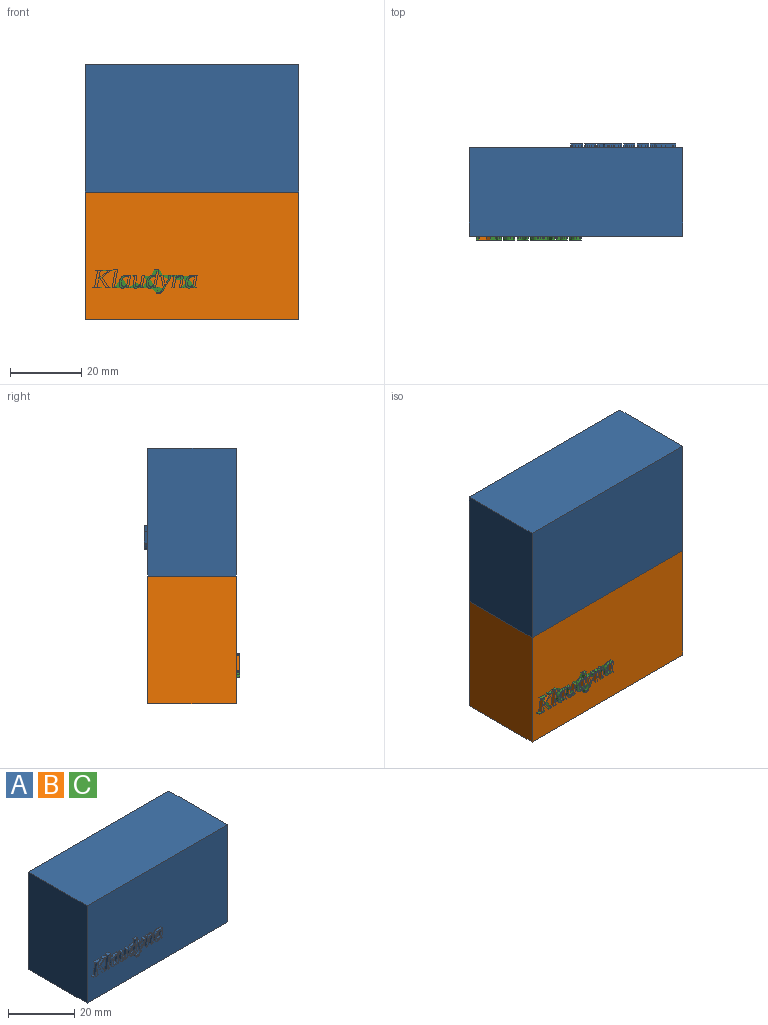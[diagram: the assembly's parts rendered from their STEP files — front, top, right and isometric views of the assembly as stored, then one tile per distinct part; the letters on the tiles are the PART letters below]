
ASSEMBLY  parts=3 mates=1
PART A: 191 faces, bbox 60x26x36 mm
  f0: plane 60x36mm, normal (0,-1,0), area 2104mm2, adj f1,f2,f3,f4,f6,f7,f8,f9
  f1: plane 60x25mm, normal (0,0,1), area 1500mm2, adj f0,f2,f4,f5
  f2: plane 36x25mm, normal (-1,0,0), area 900mm2, adj f0,f1,f3,f5
  f3: plane 60x25mm, normal (0,0,-1), area 1500mm2, adj f0,f2,f4,f5
  f4: plane 36x25mm, normal (1,0,0), area 900mm2, adj f0,f1,f3,f5
  f5: plane 60x36mm, normal (0,1,0), area 2160mm2, adj f1,f2,f3,f4
  f6: plane 1.57x1mm, normal (0,0,1), area 1.6mm2, adj f0,f7,f31,f32
  f7: plane 1x0.2mm, normal (-0.98,0,0.18), area 0.2mm2, adj f0,f6,f8,f32
  f8: plane 1x0.44mm, normal (-0.21,0,-0.98), area 0.5mm2, adj f0,f7,f9,f32
  f9: plane 2.53x2.08mm, normal (-0.64,0,0.77), area 3.3mm2, adj f0,f8,f10,f32
  f10: plane 2.08x1mm, normal (0.98,0,-0.17), area 2.1mm2, adj f0,f9,f11,f32
  f11: plane 1x0.66mm, normal (0.15,0,-0.99), area 0.7mm2, adj f0,f10,f12,f32
  f12: plane 1x0.2mm, normal (0.98,0,-0.19), area 0.2mm2, adj f0,f11,f13,f32
  f13: plane 2x1mm, normal (0,0,1), area 2mm2, adj f0,f12,f14,f32
  f14: plane 1x0.2mm, normal (-0.98,0,0.19), area 0.2mm2, adj f0,f13,f15,f32
  f15: plane 1x0.63mm, normal (-0.15,0,-0.99), area 0.6mm2, adj f0,f14,f16,f32
  f16: plane 4.41x1mm, normal (-0.98,0,0.17), area 4.5mm2, adj f0,f15,f17,f32
  f17: plane 1x0.65mm, normal (-0.15,0,0.99), area 0.7mm2, adj f0,f16,f18,f32
  f18: plane 1x0.2mm, normal (-0.98,0,0.18), area 0.2mm2, adj f0,f17,f19,f32
  f19: plane 2.08x1mm, normal (0,0,-1), area 2.1mm2, adj f0,f18,f20,f32
  f20: plane 1x0.2mm, normal (0.98,0,-0.18), area 0.2mm2, adj f0,f19,f21,f32
  f21: plane 1x0.7mm, normal (0.14,0,0.99), area 0.7mm2, adj f0,f20,f22,f32
  f22: plane 1.82x1mm, normal (0.98,0,-0.18), area 1.9mm2, adj f0,f21,f23,f32
  f23: plane 1x0.53mm, normal (0.63,0,-0.77), area 0.7mm2, adj f0,f22,f24,f32
  f24: plane 2.56x1.53mm, normal (-0.86,0,-0.51), area 3mm2, adj f0,f23,f25,f32
  f25: plane 1.15x1mm, normal (0,0,-1), area 1.1mm2, adj f0,f24,f26,f32
  f26: plane 1x0.2mm, normal (0.98,0,-0.18), area 0.2mm2, adj f0,f25,f27,f32
  f27: plane 1x0.5mm, normal (0.2,0,0.98), area 0.5mm2, adj f0,f26,f28,f32
  f28: plane 2.71x1.67mm, normal (0.85,0,0.52), area 3.2mm2, adj f0,f27,f29,f32
  f29: plane 2.07x1.7mm, normal (0.63,0,-0.77), area 2.7mm2, adj f0,f28,f30,f32
  f30: plane 1x0.58mm, normal (0.16,0,-0.99), area 0.6mm2, adj f0,f29,f31,f32
  f31: plane 1x0.2mm, normal (0.98,0,-0.18), area 0.2mm2, adj f0,f6,f30,f32
  f32: plane 5.52x5mm, normal (0,-1,0), area 8.4mm2, adj f6,f7,f8,f9,f10,f11,f12,f13
  f33: plane 5.04x1mm, normal (0.98,0,-0.17), area 5.1mm2, adj f0,f34,f40,f41
  f34: plane 1.12x1mm, normal (0,0,1), area 1.1mm2, adj f0,f33,f35,f41
  f35: plane 1x0.17mm, normal (-0.98,0,0.17), area 0.2mm2, adj f0,f34,f36,f41
  f36: plane 1x0.48mm, normal (-0.18,0,-0.98), area 0.5mm2, adj f0,f35,f37,f41
  f37: plane 5.05x1mm, normal (-0.99,0,0.17), area 5.1mm2, adj f0,f36,f38,f41
  f38: plane 1.22x1mm, normal (0,0,-1), area 1.2mm2, adj f0,f37,f39,f41
  f39: plane 1x0.17mm, normal (0.98,0,-0.17), area 0.2mm2, adj f0,f38,f40,f41
  f40: plane 1x0.59mm, normal (0.16,0,0.99), area 0.6mm2, adj f0,f33,f39,f41
  f41: plane 5.3x1.55mm, normal (0,-1,0), area 3.5mm2, adj f33,f34,f35,f36,f37,f38,f39,f40
  f42: plane 3.31x1mm, normal (0.98,0,-0.18), area 3.4mm2, adj f0,f43,f64,f65
  f43: plane 1x0.2mm, normal (0,0,1), area 0.2mm2, adj f0,f42,f44,f65
  f44: plane 1x0.17mm, normal (-0.6,0,0.8), area 0.2mm2, adj f0,f43,f45,f65
  f45: extruded ~1x0.85mm, area 0.9mm2, adj f0,f44,f46,f65
  f46: extruded ~1.04x1mm, area 1.1mm2, adj f0,f45,f47,f65
  f47: extruded ~1x0.89mm, area 1.2mm2, adj f0,f46,f48,f65
  f48: extruded ~1.22x1mm, area 1.3mm2, adj f0,f47,f49,f65
  f49: extruded ~1x0.91mm, area 1mm2, adj f0,f48,f50,f65
  f50: extruded ~1x0.73mm, area 0.8mm2, adj f0,f49,f51,f65
  f51: extruded ~1.15x1mm, area 1.4mm2, adj f0,f50,f52,f65
  f52: plane 1x0.58mm, normal (-0.98,0,0.18), area 0.6mm2, adj f0,f51,f53,f65
  f53: plane 1.06x1mm, normal (0,0,-1), area 1.1mm2, adj f0,f52,f54,f65
  f54: plane 1x0.17mm, normal (0.98,0,-0.17), area 0.2mm2, adj f0,f53,f64,f65
  f55: plane 2.22x1mm, normal (-0.98,0,0.18), area 2.3mm2, adj f56,f63,f65,f66
  f56: extruded ~1x0.92mm, area 1.1mm2, adj f55,f57,f65,f66
  f57: extruded ~1x0.45mm, area 0.5mm2, adj f56,f58,f65,f66
  f58: extruded ~1x0.64mm, area 0.7mm2, adj f57,f59,f65,f66
  f59: extruded ~1x1mm, area 1mm2, adj f58,f60,f65,f66
  f60: extruded ~1x0.76mm, area 0.9mm2, adj f59,f61,f65,f66
  f61: extruded ~1x0.68mm, area 0.8mm2, adj f60,f62,f65,f66
  f62: extruded ~1x0.31mm, area 0.3mm2, adj f61,f63,f65,f66
  f63: extruded ~1x0.27mm, area 0.3mm2, adj f55,f62,f65,f66
  f64: plane 1x0.42mm, normal (0.22,0,0.98), area 0.4mm2, adj f0,f42,f54,f65
  f65: plane 3.68x3.31mm, normal (0,-1,0), area 5.3mm2, adj f42,f43,f44,f45,f46,f47,f48,f49
  f66: plane 2.92x1.94mm, normal (0,-1,0), area 4.1mm2, adj f55,f56,f57,f58,f59,f60,f61,f62
  f67: extruded ~1x0.62mm, area 0.6mm2, adj f0,f68,f88,f89
  f68: plane 2.17x1mm, normal (0.98,0,-0.17), area 2.2mm2, adj f0,f67,f69,f89
  f69: plane 1.05x1mm, normal (0,0,1), area 1mm2, adj f0,f68,f70,f89
  f70: plane 1x0.17mm, normal (-0.98,0,0.17), area 0.2mm2, adj f0,f69,f71,f89
  f71: plane 1x0.41mm, normal (-0.21,0,-0.98), area 0.4mm2, adj f0,f70,f72,f89
  f72: extruded ~2.35x1mm, area 2.4mm2, adj f0,f71,f73,f89
  f73: extruded ~1x0.2mm, area 0.2mm2, adj f0,f72,f74,f89
  f74: extruded ~1x0.58mm, area 0.6mm2, adj f0,f73,f75,f89
  f75: extruded ~1x0.57mm, area 0.6mm2, adj f0,f74,f76,f89
  f76: extruded ~1x0.66mm, area 0.7mm2, adj f0,f75,f77,f89
  f77: extruded ~1x0.65mm, area 0.9mm2, adj f0,f76,f78,f89
  f78: plane 1x0.72mm, normal (-0.99,0,0.14), area 0.7mm2, adj f0,f77,f79,f89
  f79: plane 1.04x1mm, normal (0,0,-1), area 1mm2, adj f0,f78,f80,f89
  f80: plane 1x0.17mm, normal (0.98,0,-0.17), area 0.2mm2, adj f0,f79,f81,f89
  f81: plane 1x0.44mm, normal (0.21,0,0.98), area 0.4mm2, adj f0,f80,f82,f89
  f82: plane 3.25x1mm, normal (0.98,0,-0.17), area 3.3mm2, adj f0,f81,f83,f89
  f83: plane 1x0.62mm, normal (0,0,1), area 0.6mm2, adj f0,f82,f84,f89
  f84: plane 2.36x1mm, normal (-0.98,0,0.17), area 2.4mm2, adj f0,f83,f85,f89
  f85: extruded ~1x0.57mm, area 0.8mm2, adj f0,f84,f86,f89
  f86: extruded ~1x0.6mm, area 0.7mm2, adj f0,f85,f87,f89
  f87: extruded ~1x0.28mm, area 0.3mm2, adj f0,f86,f88,f89
  f88: extruded ~1x0.27mm, area 0.3mm2, adj f0,f67,f87,f89
  f89: plane 3.6x3.16mm, normal (0,-1,0), area 5mm2, adj f67,f68,f69,f70,f71,f72,f73,f74
  f90: extruded ~1x0.62mm, area 0.6mm2, adj f0,f91,f115,f116
  f91: extruded ~1.05x1mm, area 1.1mm2, adj f0,f90,f92,f116
  f92: extruded ~1x0.89mm, area 1.2mm2, adj f0,f91,f93,f116
  f93: extruded ~1.2x1mm, area 1.2mm2, adj f0,f92,f94,f116
  f94: extruded ~1x0.92mm, area 1mm2, adj f0,f93,f95,f116
  f95: extruded ~1x0.73mm, area 0.8mm2, adj f0,f94,f96,f116
  f96: extruded ~1.15x1mm, area 1.4mm2, adj f0,f95,f97,f116
  f97: plane 1x0.58mm, normal (-0.98,0,0.18), area 0.6mm2, adj f0,f96,f98,f116
  f98: plane 1.06x1mm, normal (0,0,-1), area 1.1mm2, adj f0,f97,f99,f116
  f99: plane 1x0.17mm, normal (0.98,0,-0.17), area 0.2mm2, adj f0,f98,f100,f116
  f100: plane 1x0.42mm, normal (0.22,0,0.98), area 0.4mm2, adj f0,f99,f101,f116
  f101: plane 5.04x1mm, normal (0.98,0,-0.17), area 5.1mm2, adj f0,f100,f102,f116
  f102: plane 1.21x1mm, normal (0,0,1), area 1.2mm2, adj f0,f101,f103,f116
  f103: plane 1x0.17mm, normal (-0.98,0,0.17), area 0.2mm2, adj f0,f102,f104,f116
  f104: plane 1x0.57mm, normal (-0.15,0,-0.99), area 0.6mm2, adj f0,f103,f115,f116
  f105: plane 2.22x1mm, normal (-0.98,0,0.18), area 2.3mm2, adj f106,f114,f116,f117
  f106: extruded ~1x0.47mm, area 0.6mm2, adj f105,f107,f116,f117
  f107: extruded ~1x0.45mm, area 0.5mm2, adj f106,f108,f116,f117
  f108: extruded ~1x0.44mm, area 0.5mm2, adj f107,f109,f116,f117
  f109: extruded ~1x0.64mm, area 0.7mm2, adj f108,f110,f116,f117
  f110: extruded ~1x1mm, area 1mm2, adj f109,f111,f116,f117
  f111: extruded ~1x0.76mm, area 0.9mm2, adj f110,f112,f116,f117
  f112: extruded ~1x0.66mm, area 0.7mm2, adj f111,f113,f116,f117
  f113: extruded ~1x0.34mm, area 0.3mm2, adj f112,f114,f116,f117
  f114: extruded ~1x0.27mm, area 0.3mm2, adj f105,f113,f116,f117
  f115: extruded ~1.53x1mm, area 1.6mm2, adj f0,f90,f104,f116
  f116: plane 5.38x3.61mm, normal (0,-1,0), area 6.5mm2, adj f90,f91,f92,f93,f94,f95,f96,f97
  f117: plane 2.92x1.94mm, normal (0,-1,0), area 4.1mm2, adj f105,f106,f107,f108,f109,f110,f111,f112
  f118: plane 1x0.17mm, normal (-0.98,0,0.17), area 0.2mm2, adj f0,f119,f141,f142
  f119: plane 1x0.42mm, normal (-0.22,0,-0.98), area 0.4mm2, adj f0,f118,f120,f142
  f120: plane 3.2x1mm, normal (-0.98,0,-0.21), area 3.3mm2, adj f0,f119,f121,f142
  f121: plane 1x0.31mm, normal (-0.88,0,0.48), area 0.3mm2, adj f0,f120,f122,f142
  f122: extruded ~1.06x1.01mm, area 1.5mm2, adj f0,f121,f123,f142
  f123: extruded ~1x0.31mm, area 0.3mm2, adj f0,f122,f124,f142
  f124: plane 1x0.36mm, normal (0.99,0,0.16), area 0.4mm2, adj f0,f123,f125,f142
  f125: plane 1x0.17mm, normal (0,0,1), area 0.2mm2, adj f0,f124,f126,f142
  f126: plane 1x0.76mm, normal (-0.98,0,0.18), area 0.8mm2, adj f0,f125,f127,f142
  f127: extruded ~1x0.56mm, area 0.6mm2, adj f0,f126,f128,f142
  f128: extruded ~1x0.53mm, area 0.6mm2, adj f0,f127,f129,f142
  f129: extruded ~1x0.49mm, area 0.7mm2, adj f0,f128,f130,f142
  f130: extruded ~1.03x1mm, area 1.2mm2, adj f0,f129,f131,f142
  f131: plane 2.49x1.48mm, normal (0.86,0,-0.51), area 2.9mm2, adj f0,f130,f132,f142
  f132: extruded ~1x0.82mm, area 0.9mm2, adj f0,f131,f133,f142
  f133: extruded ~1x0.24mm, area 0.3mm2, adj f0,f132,f134,f142
  f134: plane 1x0.71mm, normal (0,0,1), area 0.7mm2, adj f0,f133,f135,f142
  f135: plane 1x0.17mm, normal (-0.98,0,0.17), area 0.2mm2, adj f0,f134,f136,f142
  f136: extruded ~1x0.17mm, area 0.2mm2, adj f0,f135,f137,f142
  f137: extruded ~1x0.22mm, area 0.2mm2, adj f0,f136,f138,f142
  f138: extruded ~1x0.72mm, area 0.8mm2, adj f0,f137,f139,f142
  f139: plane 1.52x1mm, normal (-0.87,0,0.5), area 1.8mm2, adj f0,f138,f140,f142
  f140: plane 2.73x1mm, normal (0.98,0,0.19), area 2.8mm2, adj f0,f139,f141,f142
  f141: plane 1x0.96mm, normal (0,0,1), area 1mm2, adj f0,f118,f140,f142
  f142: plane 5.16x4.03mm, normal (0,-1,0), area 4.6mm2, adj f118,f119,f120,f121,f122,f123,f124,f125
  f143: extruded ~1x0.62mm, area 0.6mm2, adj f0,f144,f164,f165
  f144: plane 2.17x1mm, normal (-0.98,0,0.17), area 2.2mm2, adj f0,f143,f145,f165
  f145: plane 1.12x1mm, normal (0,0,-1), area 1.1mm2, adj f0,f144,f146,f165
  f146: plane 1x0.17mm, normal (0.98,0,-0.17), area 0.2mm2, adj f0,f145,f147,f165
  f147: plane 1x0.49mm, normal (0.18,0,0.98), area 0.5mm2, adj f0,f146,f148,f165
  f148: extruded ~2.4x1mm, area 2.4mm2, adj f0,f147,f149,f165
  f149: extruded ~1x0.16mm, area 0.2mm2, adj f0,f148,f150,f165
  f150: extruded ~1x0.58mm, area 0.6mm2, adj f0,f149,f151,f165
  f151: extruded ~1x0.57mm, area 0.6mm2, adj f0,f150,f152,f165
  f152: extruded ~1x0.66mm, area 0.7mm2, adj f0,f151,f153,f165
  f153: extruded ~1x0.65mm, area 0.9mm2, adj f0,f152,f154,f165
  f154: plane 1x0.72mm, normal (0.99,0,-0.14), area 0.7mm2, adj f0,f153,f155,f165
  f155: plane 1.04x1mm, normal (0,0,1), area 1mm2, adj f0,f154,f156,f165
  f156: plane 1x0.17mm, normal (-0.98,0,0.17), area 0.2mm2, adj f0,f155,f157,f165
  f157: plane 1x0.44mm, normal (-0.21,0,-0.98), area 0.4mm2, adj f0,f156,f158,f165
  f158: plane 3.25x1mm, normal (-0.98,0,0.17), area 3.3mm2, adj f0,f157,f159,f165
  f159: plane 1x0.62mm, normal (0,0,-1), area 0.6mm2, adj f0,f158,f160,f165
  f160: plane 2.35x1mm, normal (0.99,0,-0.17), area 2.4mm2, adj f0,f159,f161,f165
  f161: extruded ~1x0.58mm, area 0.8mm2, adj f0,f160,f162,f165
  f162: extruded ~1x0.6mm, area 0.7mm2, adj f0,f161,f163,f165
  f163: extruded ~1x0.28mm, area 0.3mm2, adj f0,f162,f164,f165
  f164: extruded ~1x0.27mm, area 0.3mm2, adj f0,f143,f163,f165
  f165: plane 3.6x3.23mm, normal (0,-1,0), area 5mm2, adj f143,f144,f145,f146,f147,f148,f149,f150
  f166: plane 3.31x1mm, normal (0.98,0,-0.18), area 3.4mm2, adj f0,f167,f188,f189
  f167: plane 1x0.2mm, normal (0,0,1), area 0.2mm2, adj f0,f166,f168,f189
  f168: plane 1x0.17mm, normal (-0.6,0,0.8), area 0.2mm2, adj f0,f167,f169,f189
  f169: extruded ~1x0.85mm, area 0.9mm2, adj f0,f168,f170,f189
  f170: extruded ~1.04x1mm, area 1.1mm2, adj f0,f169,f171,f189
  f171: extruded ~1x0.89mm, area 1.2mm2, adj f0,f170,f172,f189
  f172: extruded ~1.22x1mm, area 1.3mm2, adj f0,f171,f173,f189
  f173: extruded ~1x0.91mm, area 1mm2, adj f0,f172,f174,f189
  f174: extruded ~1x0.73mm, area 0.8mm2, adj f0,f173,f175,f189
  f175: extruded ~1.15x1mm, area 1.4mm2, adj f0,f174,f176,f189
  f176: plane 1x0.58mm, normal (-0.98,0,0.18), area 0.6mm2, adj f0,f175,f177,f189
  f177: plane 1.06x1mm, normal (0,0,-1), area 1.1mm2, adj f0,f176,f178,f189
  f178: plane 1x0.17mm, normal (0.98,0,-0.17), area 0.2mm2, adj f0,f177,f188,f189
  f179: plane 2.22x1mm, normal (-0.98,0,0.18), area 2.3mm2, adj f180,f187,f189,f190
  f180: extruded ~1x0.92mm, area 1.1mm2, adj f179,f181,f189,f190
  f181: extruded ~1x0.45mm, area 0.5mm2, adj f180,f182,f189,f190
  f182: extruded ~1x0.64mm, area 0.7mm2, adj f181,f183,f189,f190
  f183: extruded ~1x1mm, area 1mm2, adj f182,f184,f189,f190
  f184: extruded ~1x0.76mm, area 0.9mm2, adj f183,f185,f189,f190
  f185: extruded ~1x0.68mm, area 0.8mm2, adj f184,f186,f189,f190
  f186: extruded ~1x0.31mm, area 0.3mm2, adj f185,f187,f189,f190
  f187: extruded ~1x0.27mm, area 0.3mm2, adj f179,f186,f189,f190
  f188: plane 1x0.42mm, normal (0.22,0,0.98), area 0.4mm2, adj f0,f166,f178,f189
  f189: plane 3.68x3.31mm, normal (0,-1,0), area 5.3mm2, adj f166,f167,f168,f169,f170,f171,f172,f173
  f190: plane 2.92x1.94mm, normal (0,-1,0), area 4.1mm2, adj f179,f180,f181,f182,f183,f184,f185,f186
PART B: same geometry as A
PART C: same geometry as A
PLACE A rot(axis=(0,0,1),180deg) t=(60,-25,36)mm
PLACE B at identity fixed
PLACE C at identity
MATE fastened B.f1 <-> A.f3  axis (0,0,1) through (30,-12.5,36)mm
